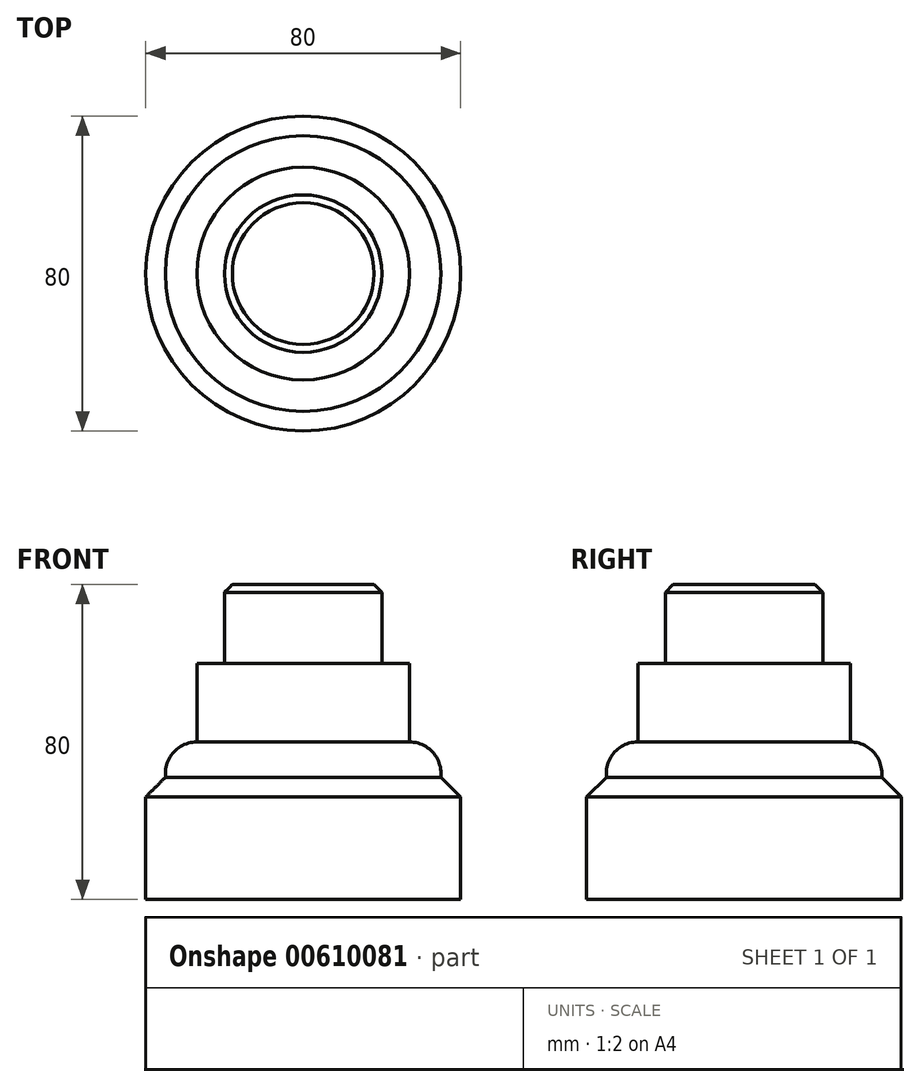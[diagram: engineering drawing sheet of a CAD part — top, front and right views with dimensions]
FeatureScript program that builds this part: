
annotation { "Feature Type Name" : "Feature", "Feature Type Description" : "" }
export const myFeature = defineFeature(function(context is Context, id is Id, definition is map)
    precondition{}
    {
        {
            var Q0;
            Q0=qCreatedBy(makeId("Front.planeOp"),FACE);
            var sketch = newSketch(context, id + "F0", { "sketchPlane" : qUnion([Q0])});
            skLineSegment(sketch, "E0.bottom", {"start": v(0, 0) * mm, "end": v(40, 0) * mm});
            skLineSegment(sketch, "E0.top", {"start": v(0, 26) * mm, "end": v(40, 26) * mm});
            skLineSegment(sketch, "E0.left", {"start": v(0, 0) * mm, "end": v(0, 26) * mm});
            skLineSegment(sketch, "E0.right", {"start": v(40, 0) * mm, "end": v(40, 26) * mm});
            skLineSegment(sketch, "E1", {"start": v(35, 31) * mm, "end": v(40, 26) * mm});
            skLineSegment(sketch, "E2", {"start": v(35, 31) * mm, "end": v(0, 31) * mm});
            skLineSegment(sketch, "E3", {"start": v(0, 31) * mm, "end": v(0, 26) * mm});
            skLineSegment(sketch, "E4.top", {"start": v(27, 40) * mm, "end": v(0, 40) * mm});
            skLineSegment(sketch, "E4.left", {"start": v(35, 31) * mm, "end": v(35, 32) * mm});
            skLineSegment(sketch, "E4.right", {"start": v(0, 31) * mm, "end": v(0, 40) * mm});
            skPoint(sketch, "E5.visualSharp", {"position": v(35, 40) * mm});
            skArc(sketch, "E5.filletArc", {"start": v(35, 32) * mm, "mid": v(32.66, 37.66) * mm, "end": v(27, 40) * mm});
            skLineSegment(sketch, "E6.top", {"start": v(27, 60) * mm, "end": v(0, 60) * mm});
            skLineSegment(sketch, "E6.left", {"start": v(27, 40) * mm, "end": v(27, 60) * mm});
            skLineSegment(sketch, "E6.right", {"start": v(0, 40) * mm, "end": v(0, 60) * mm});
            skLineSegment(sketch, "E7.bottom", {"start": v(20, 60) * mm, "end": v(0, 60) * mm});
            skLineSegment(sketch, "E7.top", {"start": v(20, 78) * mm, "end": v(0, 78) * mm});
            skLineSegment(sketch, "E7.left", {"start": v(20, 60) * mm, "end": v(20, 78) * mm});
            skLineSegment(sketch, "E7.right", {"start": v(0, 60) * mm, "end": v(0, 78) * mm});
            skLineSegment(sketch, "E8", {"start": v(18, 80) * mm, "end": v(20, 78) * mm});
            skLineSegment(sketch, "E9", {"start": v(18, 80) * mm, "end": v(0, 80) * mm});
            skLineSegment(sketch, "E10", {"start": v(0, 80) * mm, "end": v(0, 78) * mm});
            skLineSegment(sketch, "E11", {"start": v(0, 0) * mm, "end": v(0, 80) * mm});
            skSolve(sketch);
        }
        {
            var Q0;
            Q0 = qSketchRegion(id + "F0", true);
            var Q1;
            Q1=sQuery(id+"F0.wireOp",EDGE,"E11");
            revolve(context, id + "F1", {"entities" : qUnion([Q0]), "axis" : qUnion([Q1]), "revolveType" : RevolveType.FULL});
        }
    });
